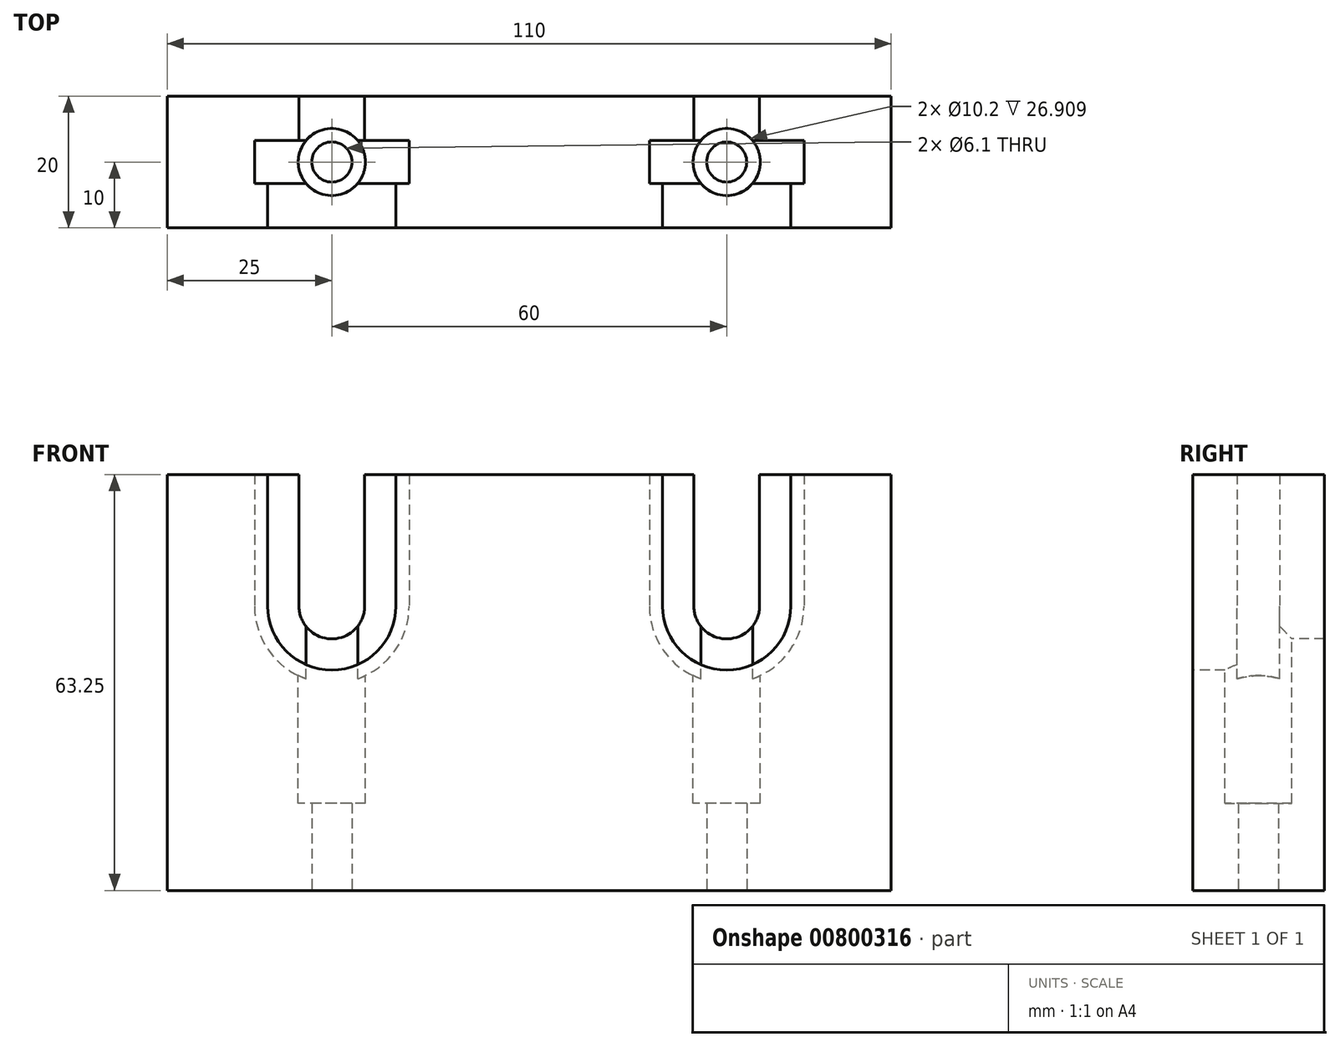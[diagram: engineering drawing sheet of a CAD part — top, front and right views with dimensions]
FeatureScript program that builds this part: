
annotation { "Feature Type Name" : "Feature", "Feature Type Description" : "" }
export const myFeature = defineFeature(function(context is Context, id is Id, definition is map)
    precondition{}
    {
        {
            var Q0;
            Q0=qCreatedBy(makeId("Front.planeOp"),FACE);
            var sketch = newSketch(context, id + "F0", { "sketchPlane" : qUnion([Q0])});
            skLineSegment(sketch, "E0.bottom", {"start": v(0, 0) * mm, "end": v(110, 0) * mm});
            skLineSegment(sketch, "E0.top", {"start": v(0, 63.25) * mm, "end": v(110, 63.25) * mm});
            skLineSegment(sketch, "E0.left", {"start": v(0, 0) * mm, "end": v(0, 63.25) * mm});
            skLineSegment(sketch, "E0.right", {"start": v(110, 0) * mm, "end": v(110, 63.25) * mm});
            skSolve(sketch);
        }
        {
            var Q0;
            Q0 = qSketchRegion(id + "F0", true);
            extrude(context, id + "F1", {"entities" : qUnion([Q0]), "depth" : 20 * mm, "offsetDistance" : 25.4 * mm});
        }
        {
            var Q0;
            Q0=makeQuery(id+"F1.opExtrude","CAP_FACE",FACE,{"disambiguationData":[OSD([sQuery(id+"F0.wireOp",EDGE,"E0.bottom"),sQuery(id+"F0.wireOp",EDGE,"E0.top"),sQuery(id+"F0.wireOp",EDGE,"E0.left"),sQuery(id+"F0.wireOp",EDGE,"E0.right")])],"isStart":false});
            var sketch = newSketch(context, id + "F2", { "sketchPlane" : qUnion([Q0])});
            skCircle(sketch, "E1", {"center": v(25, 43.25) * mm, "radius": 9.75 * mm});
            skCircle(sketch, "E2", {"center": v(85, 43.25) * mm, "radius": 9.75 * mm});
            skSolve(sketch);
        }
        {
            var Q0;
            Q0 = qSketchRegion(id + "F2", true);
            extrude(context, id + "F3", {"entities" : qUnion([Q0]), "operationType" : NewBodyOperationType.REMOVE, "oppositeDirection" : true, "depth" : 6.75 * mm, "offsetDistance" : 25.4 * mm});
        }
        {
            var Q0;
            Q0=makeQuery(id+"F3.boolean.opBoolean","COPY",FACE,{"derivedFrom":makeQuery(id+"F3.opExtrude","CAP_FACE",FACE,{"disambiguationData":[OSD([sQuery(id+"F2.wireOp",EDGE,"E1")])],"isStart":false})});
            var sketch = newSketch(context, id + "F4", { "sketchPlane" : qUnion([Q0])});
            skCircle(sketch, "E3", {"center": v(25, 43.25) * mm, "radius": 11.75 * mm});
            skCircle(sketch, "E4", {"center": v(85, 43.25) * mm, "radius": 11.75 * mm});
            skSolve(sketch);
        }
        {
            var Q0;
            Q0 = qSketchRegion(id + "F4", true);
            extrude(context, id + "F5", {"entities" : qUnion([Q0]), "operationType" : NewBodyOperationType.REMOVE, "oppositeDirection" : true, "depth" : 6.5 * mm, "offsetDistance" : 25.4 * mm});
        }
        {
            var Q0;
            Q0=makeQuery(id+"F5.boolean.opBoolean","COPY",FACE,{"derivedFrom":makeQuery(id+"F5.opExtrude","CAP_FACE",FACE,{"disambiguationData":[OSD([sQuery(id+"F4.wireOp",EDGE,"E3")])],"isStart":false})});
            var sketch = newSketch(context, id + "F6", { "sketchPlane" : qUnion([Q0])});
            skCircle(sketch, "E5", {"center": v(25, 43.25) * mm, "radius": 5 * mm});
            skCircle(sketch, "E6", {"center": v(85, 43.25) * mm, "radius": 5 * mm});
            skSolve(sketch);
        }
        {
            var Q0;
            Q0 = qSketchRegion(id + "F6", true);
            extrude(context, id + "F7", {"entities" : qUnion([Q0]), "operationType" : NewBodyOperationType.REMOVE, "endBound" : BoundingType.UP_TO_NEXT, "oppositeDirection" : true, "depth" : 25.4 * mm, "offsetDistance" : 25.4 * mm});
        }
        {
            var Q0;
            Q0=makeQuery(id+"F1.opExtrude","CAP_FACE",FACE,{"disambiguationData":[OSD([sQuery(id+"F0.wireOp",EDGE,"E0.bottom"),sQuery(id+"F0.wireOp",EDGE,"E0.top"),sQuery(id+"F0.wireOp",EDGE,"E0.left"),sQuery(id+"F0.wireOp",EDGE,"E0.right")])],"isStart":false});
            var sketch = newSketch(context, id + "F8", { "sketchPlane" : qUnion([Q0])});
            skLineSegment(sketch, "E7.bottom", {"start": v(15.25, 63.25) * mm, "end": v(34.75, 63.25) * mm});
            skLineSegment(sketch, "E7.top", {"start": v(15.25, 43.25) * mm, "end": v(34.75, 43.25) * mm});
            skLineSegment(sketch, "E7.left", {"start": v(15.25, 63.25) * mm, "end": v(15.25, 43.25) * mm});
            skLineSegment(sketch, "E7.right", {"start": v(34.75, 63.25) * mm, "end": v(34.75, 43.25) * mm});
            skLineSegment(sketch, "E8.bottom", {"start": v(75.25, 63.25) * mm, "end": v(94.75, 63.25) * mm});
            skLineSegment(sketch, "E8.top", {"start": v(75.25, 43.25) * mm, "end": v(94.75, 43.25) * mm});
            skLineSegment(sketch, "E8.left", {"start": v(75.25, 63.25) * mm, "end": v(75.25, 43.25) * mm});
            skLineSegment(sketch, "E8.right", {"start": v(94.75, 63.25) * mm, "end": v(94.75, 43.25) * mm});
            skSolve(sketch);
        }
        {
            var Q0;
            Q0 = qSketchRegion(id + "F8", true);
            var Q1;
            Q1 = qSketchRegion(id + "F6", true);
            extrude(context, id + "F9", {"entities" : qUnion([Q0, Q1]), "operationType" : NewBodyOperationType.REMOVE, "oppositeDirection" : true, "depth" : 6.75 * mm, "offsetDistance" : 25.4 * mm});
        }
        {
            var Q0;
            Q0=makeQuery(id+"F9.boolean.opBoolean","COPY",FACE,{"derivedFrom":makeQuery(id+"F9.opExtrude","CAP_FACE",FACE,{"disambiguationData":[OSD([sQuery(id+"F8.wireOp",EDGE,"E7.bottom"),sQuery(id+"F8.wireOp",EDGE,"E7.top"),sQuery(id+"F8.wireOp",EDGE,"E7.left"),sQuery(id+"F8.wireOp",EDGE,"E7.right")])],"isStart":false})});
            var sketch = newSketch(context, id + "F10", { "sketchPlane" : qUnion([Q0])});
            skLineSegment(sketch, "E9.bottom", {"start": v(13.25, 63.25) * mm, "end": v(36.75, 63.25) * mm});
            skLineSegment(sketch, "E9.top", {"start": v(13.25, 43.25) * mm, "end": v(36.75, 43.25) * mm});
            skLineSegment(sketch, "E9.left", {"start": v(13.25, 63.25) * mm, "end": v(13.25, 43.25) * mm});
            skLineSegment(sketch, "E9.right", {"start": v(36.75, 63.25) * mm, "end": v(36.75, 43.25) * mm});
            skLineSegment(sketch, "E10.bottom", {"start": v(73.25, 63.25) * mm, "end": v(96.75, 63.25) * mm});
            skLineSegment(sketch, "E10.top", {"start": v(73.25, 43.25) * mm, "end": v(96.75, 43.25) * mm});
            skLineSegment(sketch, "E10.left", {"start": v(73.25, 63.25) * mm, "end": v(73.25, 43.25) * mm});
            skLineSegment(sketch, "E10.right", {"start": v(96.75, 63.25) * mm, "end": v(96.75, 43.25) * mm});
            skSolve(sketch);
        }
        {
            var Q0;
            Q0 = qSketchRegion(id + "F10", true);
            extrude(context, id + "F11", {"entities" : qUnion([Q0]), "operationType" : NewBodyOperationType.REMOVE, "oppositeDirection" : true, "depth" : 6.5 * mm, "offsetDistance" : 25.4 * mm});
        }
        {
            var Q0;
            Q0=makeQuery(id+"F11.boolean.opBoolean","MERGE",FACE,{"derivedFrom":[makeQuery(id+"F5.boolean.opBoolean","COPY",FACE,{"derivedFrom":makeQuery(id+"F5.opExtrude","CAP_FACE",FACE,{"disambiguationData":[OSD([sQuery(id+"F4.wireOp",EDGE,"E3")])],"isStart":false})}),makeQuery(id+"F11.opExtrude","CAP_FACE",FACE,{"disambiguationData":[OSD([sQuery(id+"F10.wireOp",EDGE,"E9.bottom"),sQuery(id+"F10.wireOp",EDGE,"E9.top"),sQuery(id+"F10.wireOp",EDGE,"E9.left"),sQuery(id+"F10.wireOp",EDGE,"E9.right")])],"isStart":false})]});
            var sketch = newSketch(context, id + "F12", { "sketchPlane" : qUnion([Q0])});
            skLineSegment(sketch, "E11.bottom", {"start": v(20, 63.25) * mm, "end": v(30, 63.25) * mm});
            skLineSegment(sketch, "E11.top", {"start": v(20, 43.25) * mm, "end": v(30, 43.25) * mm});
            skLineSegment(sketch, "E11.left", {"start": v(20, 63.25) * mm, "end": v(20, 43.25) * mm});
            skLineSegment(sketch, "E11.right", {"start": v(30, 63.25) * mm, "end": v(30, 43.25) * mm});
            skLineSegment(sketch, "E12.bottom", {"start": v(80, 63.25) * mm, "end": v(90, 63.25) * mm});
            skLineSegment(sketch, "E12.top", {"start": v(80, 43.25) * mm, "end": v(90, 43.25) * mm});
            skLineSegment(sketch, "E12.left", {"start": v(80, 63.25) * mm, "end": v(80, 43.25) * mm});
            skLineSegment(sketch, "E12.right", {"start": v(90, 63.25) * mm, "end": v(90, 43.25) * mm});
            skSolve(sketch);
        }
        {
            var Q0;
            Q0 = qSketchRegion(id + "F12", true);
            extrude(context, id + "F13", {"entities" : qUnion([Q0]), "operationType" : NewBodyOperationType.REMOVE, "endBound" : BoundingType.UP_TO_NEXT, "oppositeDirection" : true, "depth" : 25.4 * mm, "offsetDistance" : 25.4 * mm});
        }
        {
            var Q0;
            {var subQ3=sQuery(id+"F0.wireOp",EDGE,"E0.top");Q0=makeQuery(id+"F13.boolean.opBoolean","SPLIT",FACE,{"disambiguationData":[TD([makeQuery(id+"F9.boolean.opBoolean","COPY",FACE,{"derivedFrom":makeQuery(id+"F9.opExtrude","SWEPT_FACE",FACE,{"disambiguationData":[OSD([sQuery(id+"F8.wireOp",EDGE,"E7.right")])]})})])],"derivedFrom":makeQuery(id+"F1.opExtrude","SWEPT_FACE",FACE,{"disambiguationData":[OSD([subQ3])]})});}
            var sketch = newSketch(context, id + "F14", { "sketchPlane" : qUnion([Q0])});
            skCircle(sketch, "E13", {"center": v(25, -10) * mm, "radius": 5.1 * mm});
            skCircle(sketch, "E14", {"center": v(85, -10) * mm, "radius": 5.1 * mm});
            skSolve(sketch);
        }
        {
            var Q0;
            Q0 = qSketchRegion(id + "F14", true);
            extrude(context, id + "F15", {"entities" : qUnion([Q0]), "operationType" : NewBodyOperationType.REMOVE, "oppositeDirection" : true, "depth" : 50 * mm, "offsetDistance" : 25.4 * mm});
        }
        {
            var Q0;
            Q0=makeQuery(id+"F1.opExtrude","SWEPT_FACE",FACE,{"disambiguationData":[OSD([sQuery(id+"F0.wireOp",EDGE,"E0.bottom")])]});
            var sketch = newSketch(context, id + "F16", { "sketchPlane" : qUnion([Q0])});
            skCircle(sketch, "E15", {"center": v(25, 10) * mm, "radius": 3.05 * mm});
            skCircle(sketch, "E16", {"center": v(85, 10) * mm, "radius": 3.05 * mm});
            skSolve(sketch);
        }
        {
            var Q0;
            Q0 = qSketchRegion(id + "F16", true);
            extrude(context, id + "F17", {"entities" : qUnion([Q0]), "operationType" : NewBodyOperationType.REMOVE, "endBound" : BoundingType.UP_TO_NEXT, "oppositeDirection" : true, "depth" : 25.4 * mm, "offsetDistance" : 25.4 * mm});
        }
    });
